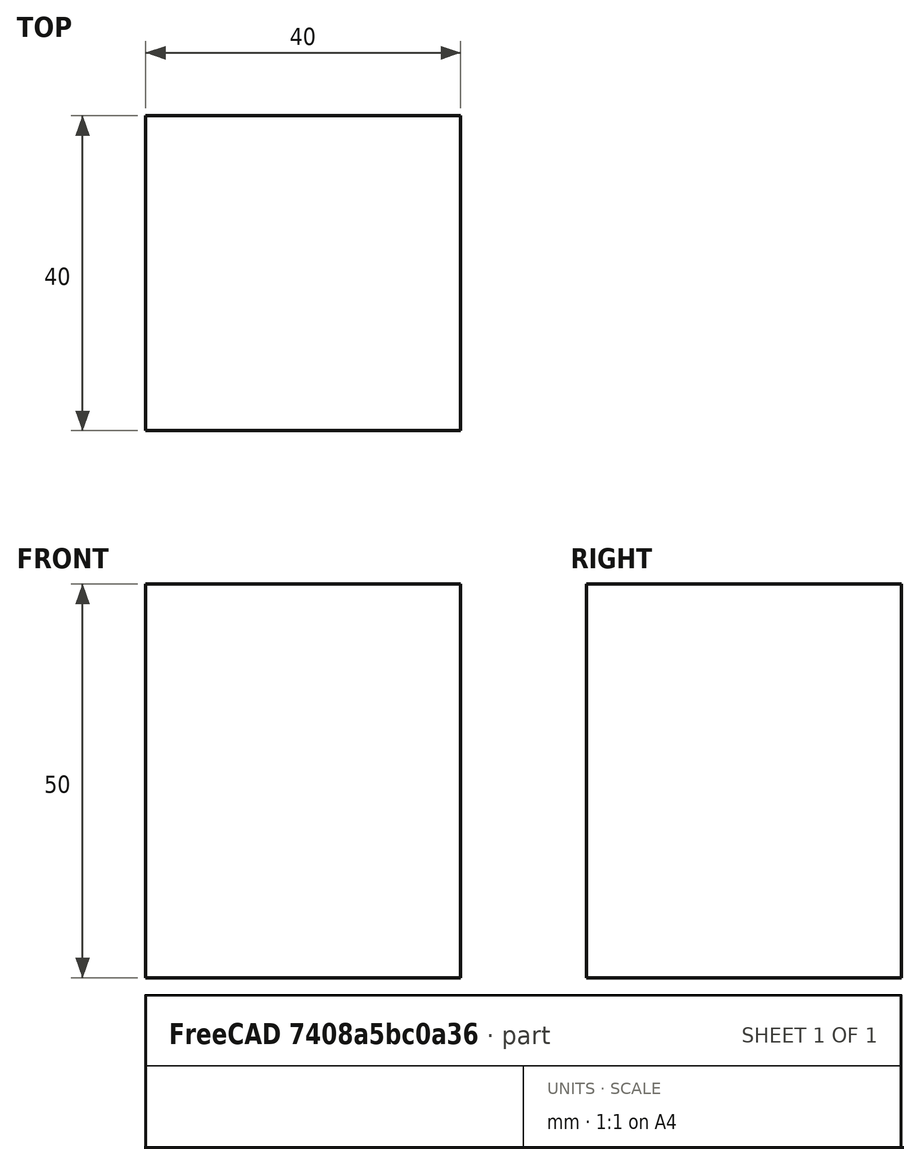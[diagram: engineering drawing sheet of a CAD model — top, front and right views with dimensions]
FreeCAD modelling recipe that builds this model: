
FCSTD DOCUMENT  (FreeCAD 0.15R4671 (Git))
Label: Square Bar 40 EN10059 S235JR
License: All rights reserved
LicenseURL: http://en.wikipedia.org/wiki/All_rights_reserved
objects: Sketcher::SketchObject×1, Part::Extrusion×1
note: 2 computed .brp shape members not serialized (recipe doc carries the construction recipe); baked Part::Feature solids carry a one-line shape summary decoded from their .brp

FEATURE [Sketcher::SketchObject] Sketch
  sketch-geometry (4):
    g0: LineSegment StartX=-20 StartY=-20 StartZ=0 EndX=20 EndY=-20 EndZ=0
    g1: LineSegment StartX=20 StartY=-20 StartZ=0 EndX=20 EndY=20 EndZ=0
    g2: LineSegment StartX=20 StartY=20 StartZ=0 EndX=-20 EndY=20 EndZ=0
    g3: LineSegment StartX=-20 StartY=20 StartZ=0 EndX=-20 EndY=-20 EndZ=0
  constraints (12):
    c: Coincident(g0,g1)
    c: Coincident(g1,g2)
    c: Coincident(g2,g3)
    c: Coincident(g3,g0)
    c: Horizontal(g0)
    c: Horizontal(g2)
    c: Vertical(g1)
    c: Vertical(g3)
    c: Symmetric(g1,g0,g-1)
    c: Symmetric(g2,g1,g-2)
    c: Equal(g1,g2)
    c: DistanceY(g1) = 40
FEATURE [Part::Extrusion] Extrude  label="Square Bar 40 EN10059 S235JR"
  Base = -> Sketch
  Dir = (0,0,50)
  Solid = true
